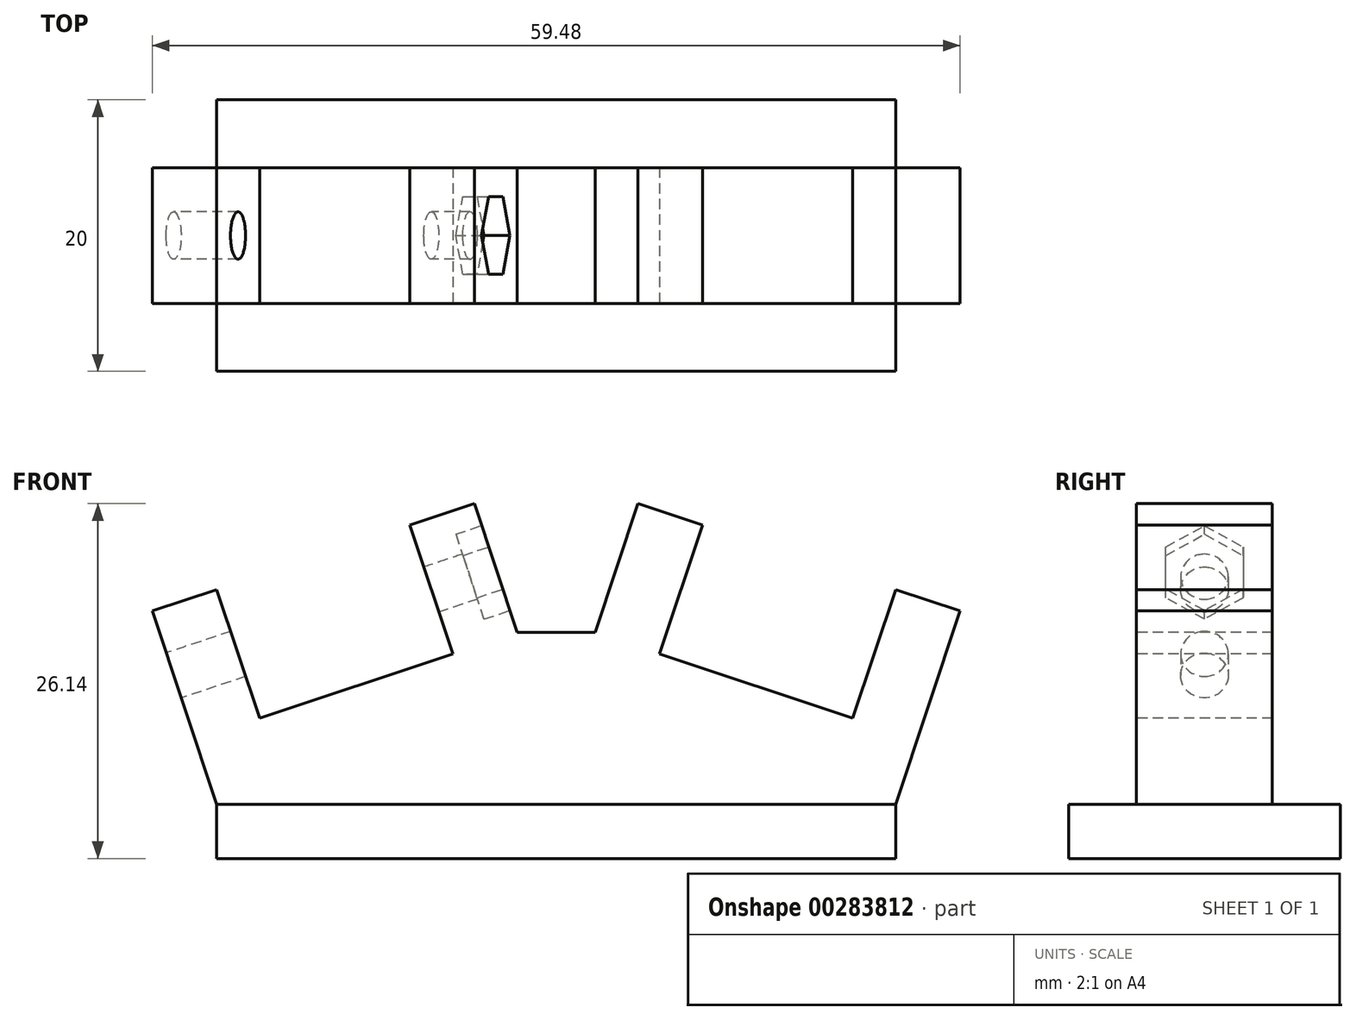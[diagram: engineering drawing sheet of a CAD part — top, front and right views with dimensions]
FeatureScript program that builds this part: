
annotation { "Feature Type Name" : "Feature", "Feature Type Description" : "" }
export const myFeature = defineFeature(function(context is Context, id is Id, definition is map)
    precondition{}
    {
        {
            var Q0;
            Q0=qCreatedBy(makeId("Top.planeOp"),FACE);
            var sketch = newSketch(context, id + "F0", { "sketchPlane" : qUnion([Q0])});
            skLineSegment(sketch, "E0.bottom", {"start": v(0, 0) * mm, "end": v(50, 0) * mm});
            skLineSegment(sketch, "E0.top", {"start": v(0, 20) * mm, "end": v(50, 20) * mm});
            skLineSegment(sketch, "E0.left", {"start": v(0, 0) * mm, "end": v(0, 20) * mm});
            skLineSegment(sketch, "E0.right", {"start": v(50, 0) * mm, "end": v(50, 20) * mm});
            skSolve(sketch);
        }
        {
            var Q0;
            Q0 = qSketchRegion(id + "F0", true);
            extrude(context, id + "F1", {"entities" : qUnion([Q0]), "depth" : 4 * mm});
        }
        {
            var Q0;
            Q0=makeQuery(id+"F1.opExtrude","SWEPT_FACE",FACE,{"disambiguationData":[OSD([sQuery(id+"F0.wireOp",EDGE,"E0.bottom")])]});
            cPlane(context, id + "F2", {"entities" : qUnion([Q0]), "cplaneType" : CPlaneType.OFFSET, "offset" : 10 * mm, "oppositeDirection" : true, "width" : 150 * mm, "height" : 150 * mm});
        }
        {
            var Q0;
            Q0=qCreatedBy(id+"F2.planeOp",FACE);
            var sketch = newSketch(context, id + "F3", { "sketchPlane" : qUnion([Q0])});
            skLineSegment(sketch, "E1.0.0", {"start": v(0, 0) * mm, "end": v(50, 0) * mm, "construction": true});
            skLineSegment(sketch, "E1.0.1", {"start": v(50, 0) * mm, "end": v(50, 4) * mm, "construction": true});
            skLineSegment(sketch, "E1.0.2", {"start": v(50, 4) * mm, "end": v(0, 4) * mm, "construction": true});
            skLineSegment(sketch, "E1.0.3", {"start": v(0, 4) * mm, "end": v(0, 0) * mm, "construction": true});
            skLineSegment(sketch, "E2", {"start": v(0, 4) * mm, "end": v(-4.74, 18.23) * mm});
            skLineSegment(sketch, "E3", {"start": v(-4.74, 18.23) * mm, "end": v(0, 19.81) * mm});
            skLineSegment(sketch, "E4", {"start": v(0, 19.81) * mm, "end": v(5.27, 4) * mm});
            skLineSegment(sketch, "E5", {"start": v(5.27, 4) * mm, "end": v(0, 4) * mm});
            skLineSegment(sketch, "E6", {"start": v(-4.74, 18.23) * mm, "end": v(25, 28.14) * mm, "construction": true});
            skPoint(sketch, "E6.endSnap0", {"position": v(25, 4) * mm});
            skLineSegment(sketch, "E7", {"start": v(21.08, 4) * mm, "end": v(14.23, 24.55) * mm});
            skLineSegment(sketch, "E8", {"start": v(14.23, 24.55) * mm, "end": v(18.97, 26.14) * mm});
            skLineSegment(sketch, "E9", {"start": v(18.97, 26.14) * mm, "end": v(25, 8.06) * mm});
            skLineSegment(sketch, "E10", {"start": v(25, 4) * mm, "end": v(25, 8.06) * mm, "construction": true});
            skLineSegment(sketch, "E11.MirrorCS", {"start": v(54.74, 18.23) * mm, "end": v(50, 19.81) * mm});
            skLineSegment(sketch, "E12.MirrorCS", {"start": v(35.77, 24.55) * mm, "end": v(31.03, 26.14) * mm});
            skLineSegment(sketch, "E13.MirrorCS", {"start": v(50, 4) * mm, "end": v(50, 0) * mm, "construction": true});
            skLineSegment(sketch, "E14.MirrorCS", {"start": v(50, 4) * mm, "end": v(54.74, 18.23) * mm});
            skLineSegment(sketch, "E15.MirrorCS", {"start": v(31.03, 26.14) * mm, "end": v(25, 8.06) * mm});
            skLineSegment(sketch, "E16.MirrorCS", {"start": v(50, 19.81) * mm, "end": v(44.73, 4) * mm});
            skLineSegment(sketch, "E17.MirrorCS", {"start": v(28.92, 4) * mm, "end": v(35.77, 24.55) * mm});
            skLineSegment(sketch, "E18.MirrorCS", {"start": v(54.74, 18.23) * mm, "end": v(25, 28.14) * mm, "construction": true});
            skLineSegment(sketch, "E19.MirrorCS", {"start": v(44.73, 4) * mm, "end": v(50, 4) * mm});
            skLineSegment(sketch, "E20", {"start": v(21.08, 4) * mm, "end": v(28.92, 4) * mm});
            skSolve(sketch);
        }
        {
            var Q0;
            Q0 = qSketchRegion(id + "F3", true);
            extrude(context, id + "F4", {"entities" : qUnion([Q0]), "operationType" : NewBodyOperationType.ADD, "endBound" : BoundingType.SYMMETRIC, "depth" : 10 * mm});
        }
        {
            var Q0;
            Q0=makeQuery(id+"F4.opExtrude","SWEPT_FACE",FACE,{"disambiguationData":[OSD([sQuery(id+"F3.wireOp",EDGE,"E2")])]});
            var sketch = newSketch(context, id + "F5", { "sketchPlane" : qUnion([Q0])});
            skCircle(sketch, "E21", {"center": v(-10, 13.8) * mm, "radius": 1.75 * mm});
            skPoint(sketch, "E21.centerSnap0", {"position": v(-10, 18.8) * mm});
            skSolve(sketch);
        }
        {
            var Q0;
            Q0 = qSketchRegion(id + "F5", true);
            var Q1;
            Q1=makeQuery(id+"F4.opExtrude","SWEPT_FACE",FACE,{"disambiguationData":[OSD([sQuery(id+"F3.wireOp",EDGE,"E9")])]});
            extrude(context, id + "F6", {"entities" : qUnion([Q0]), "operationType" : NewBodyOperationType.REMOVE, "endBound" : BoundingType.UP_TO_SURFACE, "oppositeDirection" : true, "endBoundEntityFace" : qUnion([Q1]), "depth" : 25 * mm});
        }
        {
            var Q0;
            Q0=makeQuery(id+"F4.opExtrude","SWEPT_FACE",FACE,{"disambiguationData":[OSD([sQuery(id+"F3.wireOp",EDGE,"E9")])]});
            var sketch = newSketch(context, id + "F7", { "sketchPlane" : qUnion([Q0])});
            skCircle(sketch, "E22.cCircle", {"center": v(10, 13.8) * mm, "radius": 2.85 * mm, "construction": true});
            skLineSegment(sketch, "E22.0", {"start": v(12.85, 15.44) * mm, "end": v(12.85, 12.15) * mm});
            skLineSegment(sketch, "E22.1", {"start": v(12.85, 12.15) * mm, "end": v(10, 10.5) * mm});
            skLineSegment(sketch, "E22.2", {"start": v(10, 10.5) * mm, "end": v(7.15, 12.15) * mm});
            skLineSegment(sketch, "E22.3", {"start": v(7.15, 12.15) * mm, "end": v(7.15, 15.44) * mm});
            skLineSegment(sketch, "E22.4", {"start": v(7.15, 15.44) * mm, "end": v(10, 17.09) * mm});
            skLineSegment(sketch, "E22.5", {"start": v(10, 17.09) * mm, "end": v(12.85, 15.44) * mm});
            skPoint(sketch, "E22.0.midPoint", {"position": v(12.85, 13.8) * mm});
            skSolve(sketch);
        }
        {
            var Q0;
            Q0 = qSketchRegion(id + "F7", true);
            extrude(context, id + "F8", {"entities" : qUnion([Q0]), "operationType" : NewBodyOperationType.REMOVE, "oppositeDirection" : true, "depth" : 2 * mm});
        }
        {
            var Q0;
            Q0=makeQuery(id+"F4.opExtrude","CAP_FACE",FACE,{"disambiguationData":[OSD([sQuery(id+"F3.wireOp",EDGE,"E7"),sQuery(id+"F3.wireOp",EDGE,"E8"),sQuery(id+"F3.wireOp",EDGE,"E9"),sQuery(id+"F3.wireOp",EDGE,"E12.MirrorCS"),sQuery(id+"F3.wireOp",EDGE,"E15.MirrorCS"),sQuery(id+"F3.wireOp",EDGE,"E17.MirrorCS"),sQuery(id+"F3.wireOp",EDGE,"E20")])],"isStart":false});
            var sketch = newSketch(context, id + "F9", { "sketchPlane" : qUnion([Q0])});
            skLineSegment(sketch, "E23", {"start": v(25, 8.06) * mm, "end": v(27.86, 16.65) * mm});
            skLineSegment(sketch, "E24", {"start": v(27.86, 16.65) * mm, "end": v(22.14, 16.65) * mm});
            skLineSegment(sketch, "E25", {"start": v(22.14, 16.65) * mm, "end": v(25, 8.06) * mm});
            skLineSegment(sketch, "E26.0.0", {"start": v(25, 8.06) * mm, "end": v(18.97, 26.14) * mm, "construction": true});
            skLineSegment(sketch, "E26.0.2", {"start": v(18.97, 26.14) * mm, "end": v(25, 8.06) * mm, "construction": true});
            skPoint(sketch, "E27.0", {"position": v(19.51, 24.51) * mm});
            skPoint(sketch, "E28.0", {"position": v(21.6, 18.27) * mm});
            skSolve(sketch);
        }
        {
            var Q0;
            Q0 = qSketchRegion(id + "F9", true);
            var Q1;
            Q1=makeQuery(id+"F4.opExtrude","CAP_FACE",FACE,{"disambiguationData":[OSD([sQuery(id+"F3.wireOp",EDGE,"E7"),sQuery(id+"F3.wireOp",EDGE,"E8"),sQuery(id+"F3.wireOp",EDGE,"E9"),sQuery(id+"F3.wireOp",EDGE,"E12.MirrorCS"),sQuery(id+"F3.wireOp",EDGE,"E15.MirrorCS"),sQuery(id+"F3.wireOp",EDGE,"E17.MirrorCS"),sQuery(id+"F3.wireOp",EDGE,"E20")])],"isStart":true});
            extrude(context, id + "F10", {"entities" : qUnion([Q0]), "operationType" : NewBodyOperationType.ADD, "endBound" : BoundingType.UP_TO_SURFACE, "oppositeDirection" : true, "endBoundEntityFace" : qUnion([Q1]), "depth" : 25 * mm});
        }
        {
            var Q0;
            Q0=makeQuery(id+"F4.opExtrude","CAP_FACE",FACE,{"disambiguationData":[OSD([sQuery(id+"F3.wireOp",EDGE,"E2"),sQuery(id+"F3.wireOp",EDGE,"E3"),sQuery(id+"F3.wireOp",EDGE,"E4"),sQuery(id+"F3.wireOp",EDGE,"E5")])],"isStart":false});
            var sketch = newSketch(context, id + "F11", { "sketchPlane" : qUnion([Q0])});
            skLineSegment(sketch, "E29", {"start": v(22.14, 16.65) * mm, "end": v(3.16, 10.32) * mm, "construction": true});
            skLineSegment(sketch, "E30.0.0", {"start": v(21.08, 4) * mm, "end": v(28.92, 4) * mm, "construction": true});
            skLineSegment(sketch, "E30.0.1", {"start": v(28.92, 4) * mm, "end": v(35.77, 24.55) * mm, "construction": true});
            skLineSegment(sketch, "E30.0.2", {"start": v(35.77, 24.55) * mm, "end": v(31.03, 26.14) * mm, "construction": true});
            skLineSegment(sketch, "E30.0.3", {"start": v(31.03, 26.14) * mm, "end": v(27.86, 16.65) * mm, "construction": true});
            skLineSegment(sketch, "E30.0.4", {"start": v(27.86, 16.65) * mm, "end": v(22.14, 16.65) * mm, "construction": true});
            skLineSegment(sketch, "E30.0.5", {"start": v(22.14, 16.65) * mm, "end": v(18.97, 26.14) * mm, "construction": true});
            skLineSegment(sketch, "E30.0.6", {"start": v(18.97, 26.14) * mm, "end": v(14.23, 24.55) * mm, "construction": true});
            skLineSegment(sketch, "E30.0.7", {"start": v(14.23, 24.55) * mm, "end": v(21.08, 4) * mm, "construction": true});
            skLineSegment(sketch, "E31.0.0", {"start": v(0, 0) * mm, "end": v(50, 0) * mm, "construction": true});
            skLineSegment(sketch, "E31.0.1", {"start": v(50, 0) * mm, "end": v(50, 4) * mm, "construction": true});
            skLineSegment(sketch, "E31.0.2", {"start": v(50, 4) * mm, "end": v(0, 4) * mm, "construction": true});
            skLineSegment(sketch, "E31.0.3", {"start": v(0, 4) * mm, "end": v(0, 0) * mm, "construction": true});
            skLineSegment(sketch, "E32.0.0", {"start": v(0, 4) * mm, "end": v(5.27, 4) * mm, "construction": true});
            skLineSegment(sketch, "E33", {"start": v(3.16, 10.32) * mm, "end": v(17.4, 15.07) * mm});
            skLineSegment(sketch, "E34", {"start": v(17.4, 15.07) * mm, "end": v(21.08, 4) * mm});
            skLineSegment(sketch, "E35", {"start": v(5.27, 4) * mm, "end": v(3.16, 10.32) * mm});
            skLineSegment(sketch, "E36", {"start": v(25, 16.65) * mm, "end": v(25, 4) * mm, "construction": true});
            skLineSegment(sketch, "E37.MirrorCS", {"start": v(44.73, 4) * mm, "end": v(46.84, 10.32) * mm});
            skLineSegment(sketch, "E38.MirrorCS", {"start": v(46.84, 10.32) * mm, "end": v(32.6, 15.07) * mm});
            skLineSegment(sketch, "E39.MirrorCS", {"start": v(32.6, 15.07) * mm, "end": v(28.92, 4) * mm});
            skLineSegment(sketch, "E40.MirrorCS", {"start": v(28.92, 4) * mm, "end": v(21.08, 4) * mm, "construction": true});
            skLineSegment(sketch, "E41.MirrorCS", {"start": v(27.86, 16.65) * mm, "end": v(46.84, 10.32) * mm, "construction": true});
            skLineSegment(sketch, "E42.MirrorCS", {"start": v(27.86, 16.65) * mm, "end": v(31.03, 26.14) * mm, "construction": true});
            skLineSegment(sketch, "E43.MirrorCS", {"start": v(44.73, 4) * mm, "end": v(50, 19.81) * mm, "construction": true});
            skLineSegment(sketch, "E44.MirrorCS", {"start": v(35.77, 24.55) * mm, "end": v(28.92, 4) * mm, "construction": true});
            skLineSegment(sketch, "E45.MirrorCS", {"start": v(50, 4) * mm, "end": v(44.73, 4) * mm, "construction": true});
            skLineSegment(sketch, "E46", {"start": v(5.27, 4) * mm, "end": v(21.08, 4) * mm});
            skLineSegment(sketch, "E47", {"start": v(28.92, 4) * mm, "end": v(44.73, 4) * mm});
            skSolve(sketch);
        }
        {
            var Q0;
            Q0 = qSketchRegion(id + "F11", true);
            var Q1;
            {var subQ0=sQuery(id+"F3.wireOp",EDGE,"E20");var subQ1=sQuery(id+"F3.wireOp",EDGE,"E17.MirrorCS");var subQ2=sQuery(id+"F3.wireOp",EDGE,"E15.MirrorCS");var subQ3=sQuery(id+"F3.wireOp",EDGE,"E12.MirrorCS");var subQ4=sQuery(id+"F3.wireOp",EDGE,"E9");var subQ5=sQuery(id+"F3.wireOp",EDGE,"E8");var subQ6=sQuery(id+"F3.wireOp",EDGE,"E7");Q1=makeQuery(id+"F10.boolean.opBoolean","MERGE",FACE,{"derivedFrom":[makeQuery(id+"F4.opExtrude","CAP_FACE",FACE,{"disambiguationData":[OSD([subQ6,subQ5,subQ4,subQ3,subQ2,subQ1,subQ0])],"isStart":true}),makeQuery(id+"F10.opExtrude","CAP_FACE",FACE,{"disambiguationData":[OSD([subQ6,subQ5,subQ4,subQ3,subQ2,subQ1,subQ0])],"isStart":false})]});}
            extrude(context, id + "F12", {"entities" : qUnion([Q0]), "operationType" : NewBodyOperationType.ADD, "endBound" : BoundingType.UP_TO_SURFACE, "oppositeDirection" : true, "endBoundEntityFace" : qUnion([Q1]), "depth" : 25 * mm});
        }
    });
